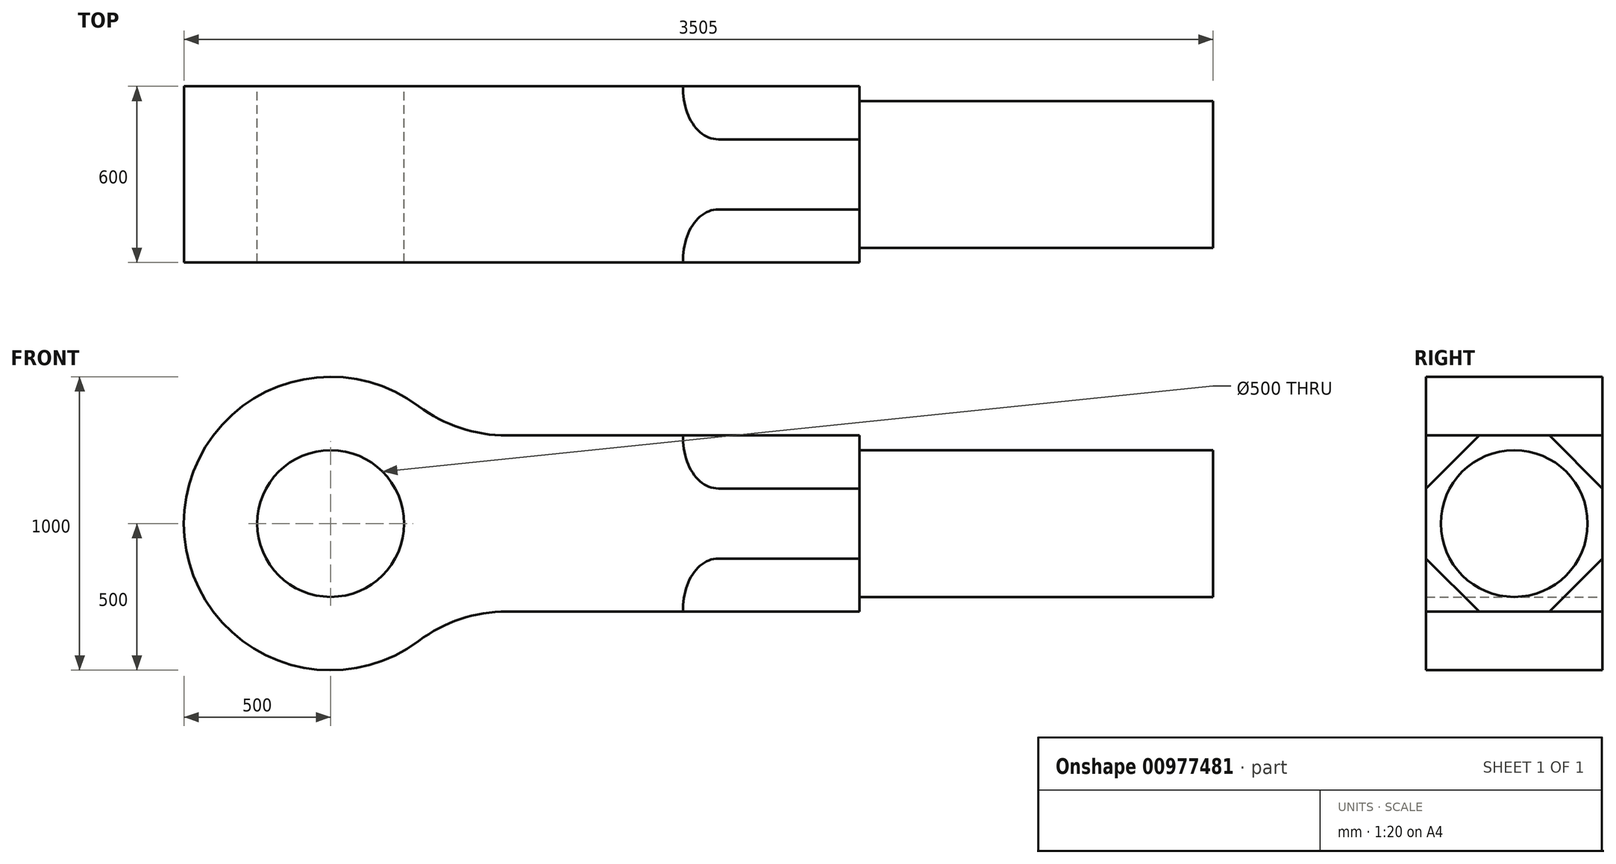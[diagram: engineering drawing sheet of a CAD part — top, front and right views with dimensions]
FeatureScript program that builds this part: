
annotation { "Feature Type Name" : "Feature", "Feature Type Description" : "" }
export const myFeature = defineFeature(function(context is Context, id is Id, definition is map)
    precondition{}
    {
        {
            var Q0;
            Q0=qCreatedBy(makeId("Front.planeOp"),FACE);
            var sketch = newSketch(context, id + "F0", { "sketchPlane" : qUnion([Q0])});
            skArc(sketch, "E0", {"start": v(300, 400) * mm, "mid": v(-500, 0) * mm, "end": v(300, -400) * mm});
            skCircle(sketch, "E1", {"center": v(0, 0) * mm, "radius": 250 * mm});
            skLineSegment(sketch, "E2", {"start": v(0, 0) * mm, "end": v(1519.98, 0) * mm, "construction": true});
            skLineSegment(sketch, "E3.bottom", {"start": v(600, 300) * mm, "end": v(1800, 300) * mm});
            skLineSegment(sketch, "E3.top", {"start": v(600, -300) * mm, "end": v(1800, -300) * mm});
            skLineSegment(sketch, "E3.right", {"start": v(1800, 300) * mm, "end": v(1800, -300) * mm});
            skPoint(sketch, "E4.visualSharp", {"position": v(400, 300) * mm});
            skArc(sketch, "E4.filletArc", {"start": v(300, 400) * mm, "mid": v(441.89, 325.66) * mm, "end": v(600, 300) * mm});
            skPoint(sketch, "E5.visualSharp", {"position": v(400, -300) * mm});
            skArc(sketch, "E5.filletArc", {"start": v(600, -300) * mm, "mid": v(441.89, -325.66) * mm, "end": v(300, -400) * mm});
            skSolve(sketch);
        }
        {
            var Q0;
            Q0 = qSketchRegion(id + "F0", true);
            extrude(context, id + "F1", {"entities" : qUnion([Q0]), "depth" : 600 * mm, "offsetDistance" : 25 * mm});
        }
        {
            var Q0;
            Q0=makeQuery(id+"F1.opExtrude","SWEPT_FACE",FACE,{"disambiguationData":[OSD([sQuery(id+"F0.wireOp",EDGE,"E3.right")])]});
            var sketch = newSketch(context, id + "F2", { "sketchPlane" : qUnion([Q0])});
            skLineSegment(sketch, "E6", {"start": v(-180.6, 300) * mm, "end": v(0, 119.4) * mm});
            skLineSegment(sketch, "E7", {"start": v(0, 119.4) * mm, "end": v(0, 300) * mm});
            skLineSegment(sketch, "E8", {"start": v(0, 300) * mm, "end": v(-180.6, 300) * mm});
            skLineSegment(sketch, "E9.1.0", {"start": v(-600, 300) * mm, "end": v(-600, 119.4) * mm});
            skLineSegment(sketch, "E9.1.1", {"start": v(-600, 119.4) * mm, "end": v(-419.4, 300) * mm});
            skLineSegment(sketch, "E9.1.2", {"start": v(-419.4, 300) * mm, "end": v(-600, 300) * mm});
            skLineSegment(sketch, "E9.2.0", {"start": v(-600, -300) * mm, "end": v(-419.4, -300) * mm});
            skLineSegment(sketch, "E9.2.1", {"start": v(-419.4, -300) * mm, "end": v(-600, -119.4) * mm});
            skLineSegment(sketch, "E9.2.2", {"start": v(-600, -119.4) * mm, "end": v(-600, -300) * mm});
            skLineSegment(sketch, "E9.3.0", {"start": v(0, -300) * mm, "end": v(0, -119.4) * mm});
            skLineSegment(sketch, "E9.3.1", {"start": v(0, -119.4) * mm, "end": v(-180.6, -300) * mm});
            skLineSegment(sketch, "E9.3.2", {"start": v(-180.6, -300) * mm, "end": v(0, -300) * mm});
            skPoint(sketch, "E9.center", {"position": v(-300, 0) * mm});
            skSolve(sketch);
        }
        {
            var Q0;
            Q0=makeQuery(id+"F2.imprint","IMPRINT",FACE,{"disambiguationData":[TD([[makeQuery(id+"F2.imprint","IMPRINT",EDGE,{"derivedFrom":sQuery(id+"F2.wireOp",EDGE,"E9.1.0")}),1.0]])]});
            var Q1;
            Q1=makeQuery(id+"F2.imprint","IMPRINT",FACE,{"disambiguationData":[TD([[makeQuery(id+"F2.imprint","IMPRINT",EDGE,{"derivedFrom":sQuery(id+"F2.wireOp",EDGE,"E6")}),1.0]])]});
            var Q2;
            Q2=makeQuery(id+"F2.imprint","IMPRINT",FACE,{"disambiguationData":[TD([[makeQuery(id+"F2.imprint","IMPRINT",EDGE,{"derivedFrom":sQuery(id+"F2.wireOp",EDGE,"E9.3.0")}),-1.0]])]});
            var Q3;
            Q3=makeQuery(id+"F2.imprint","IMPRINT",FACE,{"disambiguationData":[TD([[makeQuery(id+"F2.imprint","IMPRINT",EDGE,{"derivedFrom":sQuery(id+"F2.wireOp",EDGE,"E9.2.0")}),1.0]])]});
            extrude(context, id + "F3", {"entities" : qUnion([Q0, Q1, Q2, Q3]), "operationType" : NewBodyOperationType.REMOVE, "oppositeDirection" : true, "depth" : 600 * mm, "offsetDistance" : 25 * mm});
        }
        {
            var Q0;
            Q0=makeQuery(id+"F1.opExtrude","SWEPT_FACE",FACE,{"disambiguationData":[OSD([sQuery(id+"F0.wireOp",EDGE,"E3.right")])]});
            var sketch = newSketch(context, id + "F4", { "sketchPlane" : qUnion([Q0])});
            skCircle(sketch, "E10", {"center": v(-300, 0) * mm, "radius": 250 * mm});
            skPoint(sketch, "E10.centerSnap0", {"position": v(-300, 300) * mm});
            skSolve(sketch);
        }
        {
            var Q0;
            Q0 = qSketchRegion(id + "F4", true);
            extrude(context, id + "F5", {"entities" : qUnion([Q0]), "operationType" : NewBodyOperationType.ADD, "depth" : 1205 * mm, "offsetDistance" : 25 * mm});
        }
        {
            var Q0;
            Q0=makeQuery(id+"F3.boolean.opBoolean","COPY",EDGE,{"derivedFrom":makeQuery(id+"F3.opExtrude","CAP_EDGE",EDGE,{"disambiguationData":[OSD([sQuery(id+"F2.wireOp",EDGE,"E9.1.1")])],"isStart":false})});
            var Q1;
            Q1=makeQuery(id+"F3.boolean.opBoolean","COPY",EDGE,{"derivedFrom":makeQuery(id+"F3.opExtrude","CAP_EDGE",EDGE,{"disambiguationData":[OSD([sQuery(id+"F2.wireOp",EDGE,"E9.2.1")])],"isStart":false})});
            var Q2;
            Q2=makeQuery(id+"F3.boolean.opBoolean","COPY",EDGE,{"derivedFrom":makeQuery(id+"F3.opExtrude","CAP_EDGE",EDGE,{"disambiguationData":[OSD([sQuery(id+"F2.wireOp",EDGE,"E9.3.1")])],"isStart":false})});
            var Q3;
            Q3=makeQuery(id+"F3.boolean.opBoolean","COPY",EDGE,{"derivedFrom":makeQuery(id+"F3.opExtrude","CAP_EDGE",EDGE,{"disambiguationData":[OSD([sQuery(id+"F2.wireOp",EDGE,"E6")])],"isStart":false})});
            fillet(context, id + "F6", {"entities" : qUnion([Q0, Q1, Q2, Q3]), "radius" : 120 * mm, "tangentPropagation" : true, "allowEdgeOverflow" : false});
        }
    });
